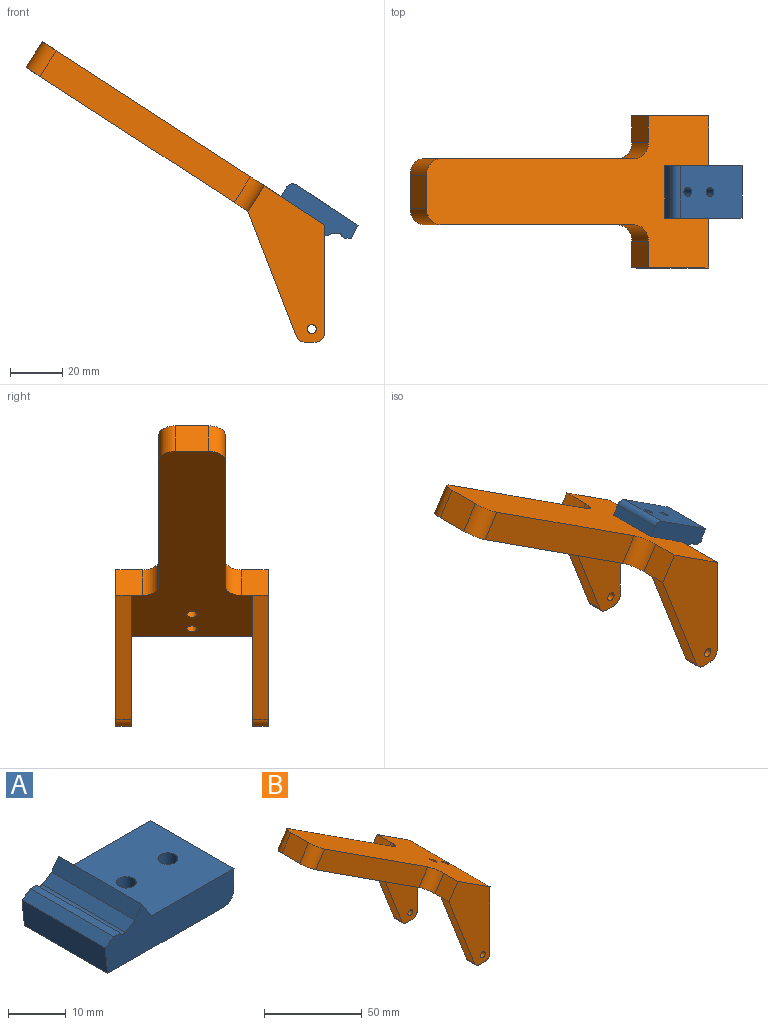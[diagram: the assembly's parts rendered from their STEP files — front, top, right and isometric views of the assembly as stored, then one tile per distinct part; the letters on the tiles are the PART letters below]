
ASSEMBLY  parts=2 mates=1
PART A: 16 faces, bbox 31.5x20.3x10.6 mm
  f0: plane 20.32x2.3mm, normal (-0.54,0,0.84), area 55.6mm2, adj f4,f5,f6,f11
  f1: plane 20.32x0.26mm, normal (0.84,0,0.54), area 6.3mm2, adj f4,f5,f9,f11
  f2: plane 20.32x2.14mm, normal (-0.54,0,0.84), area 51.6mm2, adj f3,f4,f5,f9
  f3: plane 20.32x5.65mm, normal (-0.99,0,-0.11), area 115.4mm2, adj f2,f4,f5,f8
  f4: plane 31.5x10.64mm, normal (0,1,0), area 222.1mm2, adj f0,f1,f2,f3,f6,f7,f8,f9
  f5: plane 31.5x10.64mm, normal (0,-1,0), area 222.2mm2, adj f0,f1,f2,f3,f6,f7,f8,f9
  f6: plane 20.32x2.5mm, normal (-0.82,0,0.57), area 61.9mm2, adj f0,f4,f5,f15
  f7: plane 20.32x4.37mm, normal (1,0,-0.01), area 88.8mm2, adj f4,f5,f10,f14
  f8: plane 28.32x20.32mm, normal (-0.01,0,-1), area 556.7mm2, adj f3,f4,f5,f10,f12,f13
  f9: plane 20.32x1.51mm, normal (0.01,0,1), area 30.8mm2, adj f1,f2,f4,f5
  f10: cylinder r=2.54mm len=20.32mm, axis (0,-1,0), area 81.1mm2, adj f4,f5,f7,f8
  f11: cylinder r=0.8mm len=20.32mm, axis (0,-1,0), area 25.4mm2, adj f0,f1,f4,f5
  f12: cylinder r=1.73mm len=6.93mm, axis (0.01,0,1), area 75mm2, adj f8,f14
  f13: cylinder r=1.73mm len=6.93mm, axis (0.01,0,1), area 75mm2, adj f8,f14
  f14: plane 20.32x20.21mm, normal (0.01,0,1), area 391.9mm2, adj f4,f5,f7,f12,f13,f15
  f15: plane 20.32x3.63mm, normal (0.84,0,0.54), area 87.7mm2, adj f4,f5,f6,f14
PART B: 36 faces, bbox 114.8x58.4x115.3 mm
  f0: plane 50.26x29.56mm, normal (0,1,0), area 727.1mm2, adj f2,f4,f7,f8,f26,f30,f31,f33
  f1: plane 50.26x29.56mm, normal (0,-1,0), area 727.1mm2, adj f2,f11,f12,f13,f27,f28,f29,f33
  f2: plane 109.3x70.94mm, normal (-0.54,0,-0.84), area 3896.2mm2, adj f0,f1,f3,f10,f19,f20,f21,f22
  f3: plane 10.16x9.77mm, normal (-0.84,0,0.54), area 118.3mm2, adj f2,f6,f9,f22,f27
  f4: plane 41.15x19.05mm, normal (1,0,0), area 297.4mm2, adj f0,f5,f16,f17,f31,f33
  f5: plane 60.03x29.56mm, normal (0,-1,0), area 1067.3mm2, adj f4,f7,f8,f9,f10,f16,f26,f30
  f6: plane 60.03x29.56mm, normal (0,1,0), area 1067.3mm2, adj f3,f9,f11,f12,f13,f14,f27,f28
  f7: plane 5.84x3.74mm, normal (0,0,-1), area 21.8mm2, adj f0,f5,f30,f31
  f8: cylinder r=1.73mm len=5.84mm, axis (0,1,0), area 63.4mm2, adj f0,f5
  f9: plane 108.44x70.39mm, normal (0.54,0,0.84), area 4172mm2, adj f3,f5,f6,f10,f14,f16,f19,f20
  f10: plane 10.16x9.77mm, normal (-0.84,0,0.54), area 118.3mm2, adj f2,f5,f9,f23,f26
  f11: plane 5.84x3.74mm, normal (0,0,-1), area 21.8mm2, adj f1,f6,f28,f29
  f12: plane 41.15x19.05mm, normal (1,0,0), area 297.4mm2, adj f1,f6,f14,f15,f29,f33
  f13: cylinder r=1.73mm len=5.84mm, axis (0,1,0), area 63.4mm2, adj f1,f6
  f14: plane 19.05x0mm, normal (0,0,-1), area 0.1mm2, adj f6,f9,f12,f15
  f15: plane 4.32x0mm, normal (0,1,0), area 0mm2, adj f12,f14,f18,f32
  f16: plane 19.05x0mm, normal (0,0,-1), area 0.1mm2, adj f4,f5,f9,f17
  f17: plane 4.32x0mm, normal (0,-1,0), area 0mm2, adj f4,f16,f18,f32
  f18: plane 20.32x0mm, normal (0.38,0,-0.92), area 0.1mm2, adj f15,f17,f32,f33
  f19: plane 80.91x58.17mm, normal (0,-1,0), area 1035.6mm2, adj f2,f9,f23,f25
  f20: plane 80.91x58.17mm, normal (0,1,0), area 1035.6mm2, adj f2,f9,f22,f24
  f21: plane 12.7x9.77mm, normal (-0.84,0,0.54), area 147.9mm2, adj f2,f9,f24,f25
  f22: cylinder r=6.35mm len=13.23mm, axis (0.54,0,0.84), area 116.2mm2, adj f2,f3,f9,f20
  f23: cylinder r=6.35mm len=13.23mm, axis (-0.54,0,-0.84), area 116.2mm2, adj f2,f9,f10,f19
  f24: cylinder r=6.35mm len=13.23mm, axis (0.54,0,0.84), area 116.2mm2, adj f2,f9,f20,f21
  f25: cylinder r=6.35mm len=13.23mm, axis (-0.54,0,-0.84), area 116.2mm2, adj f2,f9,f19,f21
  f26: plane 47.82x18.46mm, normal (-0.93,0,-0.36), area 299.5mm2, adj f0,f5,f10,f30
  f27: plane 47.82x18.46mm, normal (-0.93,0,-0.36), area 299.5mm2, adj f1,f3,f6,f28
  f28: cylinder r=3.81mm len=5.84mm, axis (0,-1,0), area 26.8mm2, adj f1,f6,f11,f27
  f29: cylinder r=3.81mm len=5.84mm, axis (0,-1,0), area 35mm2, adj f1,f6,f11,f12
  f30: cylinder r=3.81mm len=5.84mm, axis (0,1,0), area 26.8mm2, adj f0,f5,f7,f26
  f31: cylinder r=3.81mm len=5.84mm, axis (0,-1,0), area 35mm2, adj f0,f4,f5,f7
  f32: plane 20.32x4.32mm, normal (1,0,0), area 87.7mm2, adj f9,f15,f17,f18
  f33: plane 46.74x6.01mm, normal (0.74,0,-0.67), area 380.1mm2, adj f0,f1,f2,f4,f12,f18
  f34: cylinder r=2.03mm len=11.98mm, axis (-0.54,0,-0.84), area 148.7mm2, adj f2,f9
  f35: cylinder r=2.03mm len=11.98mm, axis (-0.54,0,-0.84), area 148.7mm2, adj f2,f9
PLACE A rot(axis=(0,-1,0),147.3deg) t=(22.8,15.34,45.84)mm
PLACE B t=(9.75,15.34,0.81)mm fixed
MATE fastened B.f35 <-> A.f13  axis (0.54,0,0.84) through (-2.17,15.34,53.51)mm
